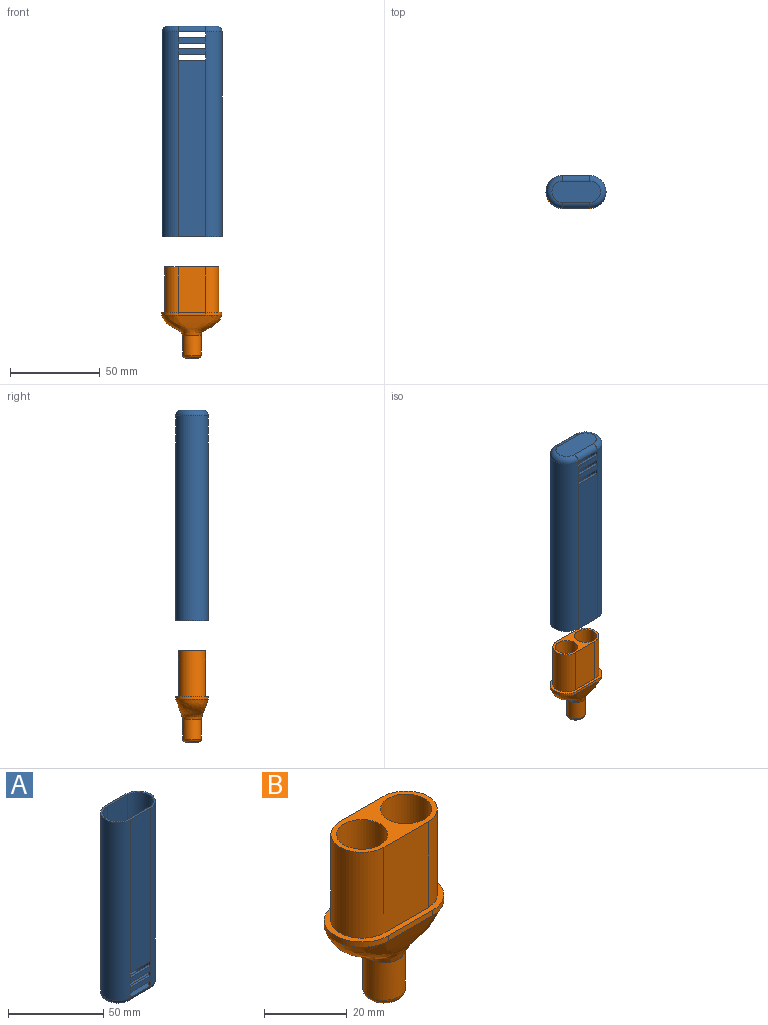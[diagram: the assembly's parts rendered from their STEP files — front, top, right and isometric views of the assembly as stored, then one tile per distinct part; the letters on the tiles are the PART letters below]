
ASSEMBLY  parts=2 mates=1
PART A: 50 faces, bbox 34.8x19.7x117.5 mm
  f0: plane 72.23x15.08mm, normal (0,-1,0), area 1088.9mm2, adj f2,f3,f37,f49
  f1: plane 72.23x15.08mm, normal (0,1,0), area 1088.9mm2, adj f2,f3,f29,f49
  f2: cylinder r=7.53mm len=88.11mm, axis (0,0,-1), area 2084.6mm2, adj f0,f1,f7,f8,f12,f13,f17,f19
  f3: cylinder r=7.53mm len=88.11mm, axis (0,0,-1), area 2084.6mm2, adj f0,f1,f7,f8,f12,f13,f17,f21
  f4: plane 33.31x18.24mm, normal (0,0,1), area 97.6mm2, adj f5,f9,f14,f16,f45,f46,f47,f48
  f5: plane 98.43x15.08mm, normal (0,-1,0), area 1483.7mm2, adj f4,f14,f16,f29
  f6: plane 15.08x3.18mm, normal (0,-1,0), area 47.9mm2, adj f14,f16,f22,f24
  f7: plane 15.08x3.18mm, normal (0,-1,0), area 47.9mm2, adj f2,f3,f32,f39
  f8: plane 15.08x3.18mm, normal (0,-1,0), area 47.9mm2, adj f2,f3,f30,f35
  f9: plane 98.43x15.08mm, normal (0,1,0), area 1483.7mm2, adj f4,f14,f16,f37
  f10: plane 15.08x3.18mm, normal (0,1,0), area 47.9mm2, adj f14,f16,f32,f39
  f11: plane 15.08x3.18mm, normal (0,1,0), area 47.9mm2, adj f14,f16,f30,f35
  f12: plane 15.08x3.18mm, normal (0,1,0), area 47.9mm2, adj f2,f3,f20,f27
  f13: plane 15.08x3.18mm, normal (0,1,0), area 47.9mm2, adj f2,f3,f22,f24
  f14: cylinder r=9.12mm len=114.3mm, axis (0,0,-1), area 3274.3mm2, adj f4,f5,f6,f9,f10,f11,f15,f19
  f15: plane 15.08x3.18mm, normal (0,-1,0), area 47.9mm2, adj f14,f16,f20,f27
  f16: cylinder r=9.12mm len=114.3mm, axis (0,0,-1), area 3274.3mm2, adj f4,f5,f6,f9,f10,f11,f15,f21
  f17: plane 30.14x18.24mm, normal (0,0,1), area 453.1mm2, adj f2,f3,f23,f25,f34,f36,f42,f43
  f18: plane 26.96x11.89mm, normal (0,0,-1), area 290.2mm2, adj f41,f42,f43,f44
  f19: plane 3.18x1.59mm, normal (1,0,0), area 5mm2, adj f2,f14,f20,f22
  f20: plane 15.08x1.59mm, normal (0,0,-1), area 23.9mm2, adj f12,f15,f19,f21
  f21: plane 3.18x1.59mm, normal (-1,0,0), area 5mm2, adj f3,f16,f20,f22
  f22: plane 15.08x1.59mm, normal (0,0,1), area 23.9mm2, adj f6,f13,f19,f21
  f23: plane 3.18x1.59mm, normal (1,0,0), area 5mm2, adj f2,f14,f17,f24
  f24: plane 15.08x1.59mm, normal (0,0,-1), area 23.9mm2, adj f6,f13,f23,f25
  f25: plane 3.18x1.59mm, normal (-1,0,0), area 5mm2, adj f3,f16,f17,f24
  f26: plane 3.18x1.59mm, normal (-1,0,0), area 5mm2, adj f3,f16,f27,f29
  f27: plane 15.08x1.59mm, normal (0,0,1), area 23.9mm2, adj f12,f15,f26,f28
  f28: plane 3.18x1.59mm, normal (1,0,0), area 5mm2, adj f2,f14,f27,f29
  f29: plane 15.08x1.59mm, normal (0,0,-1), area 23.9mm2, adj f1,f5,f26,f28
  f30: plane 15.08x1.59mm, normal (0,0,1), area 23.9mm2, adj f8,f11,f31,f33
  f31: plane 3.18x1.59mm, normal (-1,0,0), area 5mm2, adj f3,f16,f30,f32
  f32: plane 15.08x1.59mm, normal (0,0,-1), area 23.9mm2, adj f7,f10,f31,f33
  f33: plane 3.18x1.59mm, normal (1,0,0), area 5mm2, adj f2,f14,f30,f32
  f34: plane 3.18x1.59mm, normal (-1,0,0), area 5mm2, adj f3,f16,f17,f35
  f35: plane 15.08x1.59mm, normal (0,0,-1), area 23.9mm2, adj f8,f11,f34,f36
  f36: plane 3.18x1.59mm, normal (1,0,0), area 5mm2, adj f2,f14,f17,f35
  f37: plane 15.08x1.59mm, normal (0,0,-1), area 23.9mm2, adj f0,f9,f38,f40
  f38: plane 3.18x1.59mm, normal (1,0,0), area 5mm2, adj f2,f14,f37,f39
  f39: plane 15.08x1.59mm, normal (0,0,1), area 23.9mm2, adj f7,f10,f38,f40
  f40: plane 3.18x1.59mm, normal (-1,0,0), area 5mm2, adj f3,f16,f37,f39
  f41: torus R=5.94mm, axis (0,0,-1), area 124.8mm2, adj f14,f18,f42,f43
  f42: cylinder r=3.17mm len=15.08mm, axis (-1,0,0), area 75.2mm2, adj f17,f18,f41,f44
  f43: cylinder r=3.17mm len=15.08mm, axis (1,0,0), area 75.2mm2, adj f17,f18,f41,f44
  f44: torus R=5.94mm, axis (0,0,-1), area 124.8mm2, adj f16,f18,f42,f43
  f45: plane 26.19x15.08mm, normal (0,-1,0), area 394.9mm2, adj f4,f46,f48,f49
  f46: cylinder r=7.93mm len=26.19mm, axis (0,0,1), area 652.4mm2, adj f4,f45,f47,f49
  f47: plane 26.19x15.08mm, normal (0,1,0), area 394.9mm2, adj f4,f46,f48,f49
  f48: cylinder r=7.98mm len=26.19mm, axis (0,0,1), area 656.7mm2, adj f4,f45,f47,f49
  f49: plane 30.98x15.96mm, normal (0,0,1), area 33.3mm2, adj f0,f1,f2,f3,f45,f46,f47,f48
PART B: 22 faces, bbox 33.5x18.5x51 mm
  f0: cylinder r=9.12mm len=18.24mm, axis (0,0,-1), area 45.5mm2, adj f1,f3,f8,f19
  f1: plane 15.1x1.62mm, normal (0,-1,0), area 23.9mm2, adj f0,f2,f8,f19
  f2: cylinder r=9.12mm len=18.24mm, axis (0,0,-1), area 45.5mm2, adj f1,f3,f8,f19
  f3: plane 15.1x1.62mm, normal (0,1,0), area 23.9mm2, adj f0,f2,f8,f19
  f4: plane 30.12x15.06mm, normal (0,0,1), area 163.7mm2, adj f15,f16,f17,f18,f20,f21
  f5: plane 28.54x13.47mm, normal (0,0,-1), area 104.2mm2, adj f11,f12,f13,f14,f20,f21
  f6: cylinder r=5.16mm len=11.11mm, axis (0,0,1), area 360mm2, adj f8,f10
  f7: cylinder r=3.57mm len=12.7mm, axis (0,0,1), area 284.8mm2, adj f9,f10
  f8: bspline ~33.26x18.24mm, area 854.1mm2, adj f0,f1,f2,f3,f6
  f9: bspline ~28.5x13.47mm, area 642.1mm2, adj f7,f11,f12,f13,f14
  f10: torus R=3.57mm, axis (0,0,-1), area 71.7mm2, adj f6,f7
  f11: plane 15.3x1.83mm, normal (0,1,0), area 23.9mm2, adj f5,f9,f12,f14
  f12: cylinder r=6.74mm len=13.47mm, axis (0,0,-1), area 33.6mm2, adj f5,f9,f11,f13
  f13: plane 15.3x1.83mm, normal (0,-1,0), area 23.9mm2, adj f5,f9,f12,f14
  f14: cylinder r=6.74mm len=13.47mm, axis (0,0,-1), area 33.6mm2, adj f5,f9,f11,f13
  f15: cylinder r=7.53mm len=25.4mm, axis (0,0,1), area 601mm2, adj f4,f16,f18,f19
  f16: plane 25.4x15.06mm, normal (0,1,0), area 382.6mm2, adj f4,f15,f17,f19
  f17: cylinder r=7.53mm len=25.4mm, axis (0,0,1), area 601mm2, adj f4,f16,f18,f19
  f18: plane 25.4x15.06mm, normal (0,-1,0), area 382.6mm2, adj f4,f15,f17,f19
  f19: plane 33.3x18.24mm, normal (0,0,1), area 130.9mm2, adj f0,f1,f2,f3,f15,f16,f17,f18
  f20: cylinder r=6.2mm len=25.4mm, axis (0,0,1), area 989.1mm2, adj f4,f5
  f21: cylinder r=6.2mm len=25.4mm, axis (0,0,1), area 989.1mm2, adj f4,f5
PLACE A rot(axis=(1,0,0),180deg) t=(-39.92,-8.87,30.2)mm
PLACE B t=(-40.1,-8.87,-24.76)mm
MATE slider A.f4 <-> B.f6  axis (0,0,-1) through (-32.57,-8.87,17.5)mm
